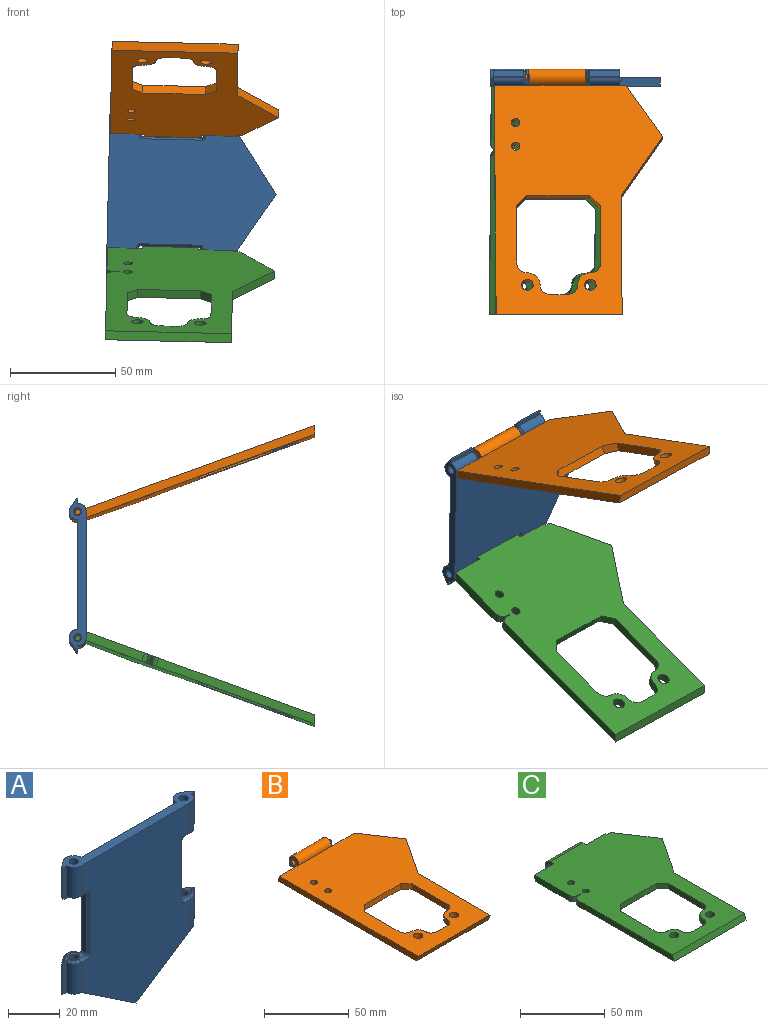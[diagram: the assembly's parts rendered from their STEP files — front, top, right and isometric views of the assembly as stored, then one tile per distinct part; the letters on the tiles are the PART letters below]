
ASSEMBLY  parts=3 mates=2
PART A: 75 faces, bbox 72.4x8x80 mm
  f0: cylinder r=4mm len=14.25mm, axis (0,0,1), area 89.5mm2, adj f4,f9,f39,f60
  f1: cylinder r=4mm len=14.25mm, axis (0,0,1), area 124.2mm2, adj f5,f20,f38,f43
  f2: cylinder r=4mm len=14.25mm, axis (0,0,1), area 89.5mm2, adj f4,f11,f35,f54
  f3: cylinder r=4mm len=14.25mm, axis (0,0,1), area 124.2mm2, adj f5,f9,f34,f45
  f4: plane 80x60mm, normal (0,-1,0), area 3886.9mm2, adj f0,f2,f7,f8,f9,f18,f21,f55
  f5: plane 80x56.3mm, normal (0,1,0), area 2940.6mm2, adj f1,f3,f8,f9,f10,f11,f12,f13
  f6: cylinder r=1.85mm len=14.75mm, axis (0,0,1), area 171.5mm2, adj f9,f27
  f7: cylinder r=4mm len=14.25mm, axis (0,0,1), area 89.5mm2, adj f4,f9,f33,f53
  f8: plane 30x20mm, normal (-0.55,0,-0.83), area 141mm2, adj f4,f5,f10,f11,f18
  f9: plane 72.36x8mm, normal (0,0,1), area 300.9mm2, adj f0,f3,f4,f5,f6,f7,f16,f17
  f10: cylinder r=1.85mm len=15.98mm, axis (0,0,1), area 173.7mm2, adj f5,f8,f11,f26
  f11: plane 10.18x8mm, normal (0,0,-1), area 33.1mm2, adj f2,f5,f8,f10,f12,f35,f36,f50
  f12: cylinder r=4mm len=14.25mm, axis (0,0,1), area 124.2mm2, adj f5,f11,f36,f47
  f13: plane 8.75x6mm, normal (0,0,-1), area 16.5mm2, adj f5,f27,f32,f33,f45,f46,f53,f55
  f14: plane 8.75x6mm, normal (0,0,1), area 16.5mm2, adj f5,f26,f31,f35,f47,f48,f54,f56
  f15: plane 28.5x3mm, normal (-1,0,0), area 85.5mm2, adj f5,f31,f32,f59
  f16: cylinder r=1.85mm len=14.75mm, axis (0,0,1), area 171.5mm2, adj f9,f28
  f17: cylinder r=4mm len=14.25mm, axis (0,0,1), area 124.2mm2, adj f5,f9,f40,f41
  f18: plane 30x20mm, normal (0.55,0,-0.83), area 141mm2, adj f4,f5,f8,f19,f20
  f19: cylinder r=1.85mm len=15.98mm, axis (0,0,1), area 173.7mm2, adj f5,f18,f20,f25
  f20: plane 10.18x8mm, normal (0,0,-1), area 33.1mm2, adj f1,f5,f18,f19,f21,f37,f38,f51
  f21: cylinder r=4mm len=14.25mm, axis (0,0,1), area 89.5mm2, adj f4,f20,f37,f61
  f22: plane 8.75x6mm, normal (0,0,-1), area 16.5mm2, adj f5,f28,f29,f39,f41,f42,f60,f62
  f23: plane 8.75x6mm, normal (0,0,1), area 16.5mm2, adj f5,f25,f30,f37,f43,f44,f61,f63
  f24: plane 28.5x3mm, normal (1,0,0), area 85.5mm2, adj f5,f29,f30,f66
  f25: cone r=2.35mm half-angle=45deg, axis (0,0,1), area 9.3mm2, adj f19,f23
  f26: cone r=1.85mm half-angle=45deg, axis (0,0,1), area 9.3mm2, adj f10,f14
  f27: cone r=2.35mm half-angle=45deg, axis (0,0,-1), area 9.3mm2, adj f6,f13
  f28: cone r=1.85mm half-angle=45deg, axis (0,0,-1), area 9.3mm2, adj f16,f22
  f29: cylinder r=0.5mm len=3mm, axis (0,1,0), area 2.4mm2, adj f5,f22,f24,f64
  f30: cylinder r=0.5mm len=3mm, axis (0,-1,0), area 2.4mm2, adj f5,f23,f24,f65
  f31: cylinder r=0.5mm len=3mm, axis (0,-1,0), area 2.4mm2, adj f5,f14,f15,f58
  f32: cylinder r=0.5mm len=3mm, axis (0,1,0), area 2.4mm2, adj f5,f13,f15,f57
  f33: plane 15.25x3mm, normal (0,-1,0), area 30.8mm2, adj f7,f9,f13,f46,f49,f53
  f34: plane 14.25x3.89mm, normal (-0.57,0.82,0), area 67.6mm2, adj f3,f9,f46,f49
  f35: plane 15.25x3mm, normal (0,-1,0), area 30.8mm2, adj f2,f11,f14,f48,f50,f54
  f36: plane 14.25x3.89mm, normal (-0.57,0.82,0), area 67.6mm2, adj f11,f12,f48,f50
  f37: plane 15.25x3mm, normal (0,-1,0), area 30.8mm2, adj f20,f21,f23,f44,f51,f61
  f38: plane 14.25x3.89mm, normal (0.57,0.82,0), area 67.6mm2, adj f1,f20,f44,f51
  f39: plane 15.25x3mm, normal (0,-1,0), area 30.8mm2, adj f0,f9,f22,f42,f52,f60
  f40: plane 14.25x3.89mm, normal (0.57,0.82,0), area 67.6mm2, adj f9,f17,f42,f52
  f41: cone r=4mm half-angle=45deg, axis (0,0,1), area 10.8mm2, adj f5,f17,f22,f42
  f42: plane 4.47x3.28mm, normal (0.4,0.58,-0.71), area 6.7mm2, adj f22,f39,f40,f41,f52
  f43: cone r=3mm half-angle=45deg, axis (0,0,-1), area 10.8mm2, adj f1,f5,f23,f44
  f44: plane 4.47x3.28mm, normal (0.4,0.58,0.71), area 6.7mm2, adj f23,f37,f38,f43,f51
  f45: cone r=3mm half-angle=45deg, axis (0,0,1), area 10.8mm2, adj f3,f5,f13,f46
  f46: plane 4.47x3.28mm, normal (-0.4,0.58,-0.71), area 6.7mm2, adj f13,f33,f34,f45,f49
  f47: cone r=4mm half-angle=45deg, axis (0,0,-1), area 10.8mm2, adj f5,f12,f14,f48
  f48: plane 4.47x3.28mm, normal (-0.4,0.58,0.71), area 6.7mm2, adj f14,f35,f36,f47,f50
  f49: plane 14.82x0.57mm, normal (-0.95,-0.3,0), area 8.7mm2, adj f9,f33,f34,f46
  f50: plane 14.82x0.57mm, normal (-0.95,-0.3,0), area 8.7mm2, adj f11,f35,f36,f48
  f51: plane 14.82x0.57mm, normal (0.95,-0.3,0), area 8.7mm2, adj f20,f37,f38,f44
  f52: plane 14.82x0.57mm, normal (0.95,-0.3,0), area 8.7mm2, adj f9,f39,f40,f42
  f53: cone r=4mm half-angle=45deg, axis (0,0,1), area 7.8mm2, adj f7,f13,f33,f55
  f54: cone r=3mm half-angle=45deg, axis (0,0,-1), area 7.8mm2, adj f2,f14,f35,f56
  f55: plane 3.5x1mm, normal (0,-0.71,-0.71), area 4.9mm2, adj f4,f13,f53,f57
  f56: plane 3.5x1mm, normal (0,-0.71,0.71), area 4.9mm2, adj f4,f14,f54,f58
  f57: cone r=1.5mm half-angle=45deg, axis (0,-1,0), area 2.2mm2, adj f4,f32,f55,f59
  f58: cone r=1.5mm half-angle=45deg, axis (0,-1,0), area 2.2mm2, adj f4,f31,f56,f59
  f59: plane 28.5x1mm, normal (-0.71,-0.71,0), area 40.3mm2, adj f4,f15,f57,f58
  f60: cone r=3mm half-angle=45deg, axis (0,0,1), area 7.8mm2, adj f0,f22,f39,f62
  f61: cone r=4mm half-angle=45deg, axis (0,0,-1), area 7.8mm2, adj f21,f23,f37,f63
  f62: plane 3.5x1mm, normal (0,-0.71,-0.71), area 4.9mm2, adj f4,f22,f60,f64
  f63: plane 3.5x1mm, normal (0,-0.71,0.71), area 4.9mm2, adj f4,f23,f61,f65
  f64: cone r=1.5mm half-angle=45deg, axis (0,-1,0), area 2.2mm2, adj f4,f29,f62,f66
  f65: cone r=1.5mm half-angle=45deg, axis (0,-1,0), area 2.2mm2, adj f4,f30,f63,f66
  f66: plane 28.5x1mm, normal (0.71,-0.71,0), area 40.3mm2, adj f4,f24,f64,f65
  f67: cylinder r=15.25mm len=30.5mm, axis (0,1,0), area 143.7mm2, adj f68,f73
  f68: cone r=15.75mm half-angle=45deg, axis (0,1,0), area 68.9mm2, adj f5,f67
  f69: plane 30.1x30.1mm, normal (0,1,0), area 626.6mm2, adj f73,f74
  f70: plane 9x9mm, normal (0,1,0), area 63.6mm2, adj f71
  f71: cone r=4.5mm half-angle=45deg, axis (0,-1,0), area 21.1mm2, adj f70,f72
  f72: cylinder r=5mm len=10mm, axis (0,1,0), area 47.1mm2, adj f71,f74
  f73: cone r=15.25mm half-angle=45deg, axis (0,1,0), area 26.9mm2, adj f67,f69
  f74: cone r=5mm half-angle=45deg, axis (0,-1,0), area 9.1mm2, adj f69,f72
PART B: 41 faces, bbox 80x124x8.2 mm
  f0: plane 8x4mm, normal (0,1,0), area 32mm2, adj f5,f13,f38,f39
  f1: plane 16.45x0.8mm, normal (0,1,0), area 13.1mm2, adj f4,f5,f19,f25
  f2: plane 8x7.96mm, normal (1,0,0), area 37.2mm2, adj f6,f13,f22,f24
  f3: plane 8x7.96mm, normal (-1,0,0), area 37.2mm2, adj f6,f13,f23,f25
  f4: plane 117.16x4mm, normal (-1,0,0), area 463mm2, adj f1,f5,f13,f19,f30
  f5: plane 116x80mm, normal (0,0,1), area 5755mm2, adj f0,f1,f4,f6,f7,f8,f9,f10
  f6: cylinder r=4mm len=27.11mm, axis (-1,0,0), area 509mm2, adj f2,f3,f5,f13,f24,f25
  f7: plane 29x4mm, normal (1,0,0), area 116mm2, adj f5,f13,f32,f40
  f8: plane 30x4mm, normal (0,-1,0), area 120mm2, adj f5,f13,f31,f32
  f9: plane 29x4mm, normal (-1,0,0), area 116mm2, adj f5,f13,f31,f37
  f10: plane 60x4mm, normal (1,0,0), area 237.1mm2, adj f5,f11,f13,f30
  f11: plane 30x20mm, normal (0.83,-0.55,0), area 144.2mm2, adj f5,f10,f12,f13
  f12: plane 26x17.33mm, normal (0.83,0.55,0), area 125mm2, adj f5,f11,f13,f14
  f13: plane 118.54x80mm, normal (0,0,-1), area 5814.2mm2, adj f0,f2,f3,f4,f6,f7,f8,f9
  f14: plane 19.11x4mm, normal (0,1,0), area 23.7mm2, adj f5,f12,f13,f20,f21,f24
  f15: cylinder r=1.5mm len=3mm, axis (-1,0,0), area 21.2mm2, adj f22,f26
  f16: plane 2.5x2.5mm, normal (1,0,0), area 4.9mm2, adj f26
  f17: cylinder r=1.5mm len=3mm, axis (1,0,0), area 21.2mm2, adj f23,f27
  f18: plane 2.5x2.5mm, normal (-1,0,0), area 4.9mm2, adj f27
  f19: plane 16x3.2mm, normal (0,0.94,0.34), area 54.5mm2, adj f1,f4,f13,f25
  f20: plane 16x3.2mm, normal (0,0.94,0.34), area 54.5mm2, adj f13,f14,f21,f24
  f21: plane 3.2x1.16mm, normal (1,0,0), area 1.9mm2, adj f13,f14,f20
  f22: torus R=2mm, axis (-1,0,0), area 8.3mm2, adj f2,f15
  f23: torus R=2mm, axis (-1,0,0), area 8.3mm2, adj f3,f17
  f24: cylinder r=0.5mm len=4.73mm, axis (0,-0.34,0.94), area 3.1mm2, adj f2,f6,f13,f14,f20
  f25: cylinder r=0.5mm len=4.73mm, axis (0,0.34,-0.94), area 3.1mm2, adj f1,f3,f6,f13,f19
  f26: cone r=1.5mm half-angle=45deg, axis (-1,0,0), area 3.1mm2, adj f15,f16
  f27: cone r=1.5mm half-angle=45deg, axis (1,0,0), area 3.1mm2, adj f17,f18
  f28: cylinder r=2mm len=4mm, axis (0,0,-1), area 50.3mm2, adj f5,f13
  f29: cylinder r=2mm len=4mm, axis (0,0,-1), area 50.3mm2, adj f5,f13
  f30: plane 60x4mm, normal (0,-0.94,-0.34), area 255.4mm2, adj f4,f5,f10,f13
  f31: plane 5x5mm, normal (-0.71,-0.71,0), area 28.3mm2, adj f5,f8,f9,f13
  f32: plane 5x5mm, normal (0.71,-0.71,0), area 28.3mm2, adj f5,f7,f8,f13
  f33: cylinder r=6mm len=6mm, axis (0,0,1), area 37.7mm2, adj f5,f13,f39,f40
  f34: cylinder r=2.75mm len=5.5mm, axis (0,0,1), area 69.1mm2, adj f5,f13
  f35: cylinder r=6mm len=6mm, axis (0,0,1), area 37.7mm2, adj f5,f13,f37,f38
  f36: cylinder r=2.75mm len=5.5mm, axis (0,0,1), area 69.1mm2, adj f5,f13
  f37: cylinder r=5mm len=5mm, axis (0,0,1), area 31.4mm2, adj f5,f9,f13,f35
  f38: cylinder r=5mm len=5mm, axis (0,0,1), area 31.4mm2, adj f0,f5,f13,f35
  f39: cylinder r=5mm len=5mm, axis (0,0,1), area 31.4mm2, adj f0,f5,f13,f33
  f40: cylinder r=5mm len=5mm, axis (0,0,1), area 31.4mm2, adj f5,f7,f13,f33
PART C: 55 faces, bbox 80x124x8.2 mm
  f0: plane 8x4mm, normal (0,1,0), area 32mm2, adj f2,f3,f49,f50
  f1: plane 29.57x4mm, normal (-1,0,0), area 115.5mm2, adj f2,f3,f6,f20,f42
  f2: plane 116x80mm, normal (0,0,-1), area 5746.4mm2, adj f0,f1,f4,f5,f6,f9,f10,f11
  f3: plane 118.54x80mm, normal (0,0,1), area 5805.6mm2, adj f0,f1,f4,f5,f7,f8,f9,f10
  f4: plane 29x4mm, normal (1,0,0), area 116mm2, adj f2,f3,f33,f51
  f5: plane 29x4mm, normal (-1,0,0), area 116mm2, adj f2,f3,f32,f48
  f6: plane 16.45x0.8mm, normal (0,1,0), area 13.1mm2, adj f1,f2,f20,f24
  f7: plane 8x7.96mm, normal (1,0,0), area 37.2mm2, adj f3,f10,f23,f26
  f8: plane 8x7.96mm, normal (-1,0,0), area 37.2mm2, adj f3,f10,f24,f25
  f9: plane 80.41x4mm, normal (-1,0,0), area 318.7mm2, adj f2,f3,f31,f41
  f10: cylinder r=4mm len=27.11mm, axis (-1,0,0), area 509mm2, adj f2,f3,f7,f8,f23,f24
  f11: plane 30x4mm, normal (0,-1,0), area 120mm2, adj f2,f3,f32,f33
  f12: plane 60x4mm, normal (1,0,0), area 237.1mm2, adj f2,f3,f13,f31
  f13: plane 30x20mm, normal (0.83,-0.55,0), area 144.2mm2, adj f2,f3,f12,f14
  f14: plane 26x17.33mm, normal (0.83,0.55,0), area 125mm2, adj f2,f3,f13,f15
  f15: plane 19.11x4mm, normal (0,1,0), area 23.7mm2, adj f2,f3,f14,f21,f22,f23
  f16: cylinder r=1.5mm len=3mm, axis (-1,0,0), area 21.2mm2, adj f26,f28
  f17: plane 2.5x2.5mm, normal (1,0,0), area 4.9mm2, adj f28
  f18: cylinder r=1.5mm len=3mm, axis (1,0,0), area 21.2mm2, adj f25,f27
  f19: plane 2.5x2.5mm, normal (-1,0,0), area 4.9mm2, adj f27
  f20: plane 16x3.2mm, normal (0,0.94,-0.34), area 54.5mm2, adj f1,f3,f6,f24
  f21: plane 16x3.2mm, normal (0,0.94,-0.34), area 54.5mm2, adj f3,f15,f22,f23
  f22: plane 3.2x1.16mm, normal (1,0,0), area 1.9mm2, adj f3,f15,f21
  f23: cylinder r=0.5mm len=4.73mm, axis (0,-0.34,-0.94), area 3.1mm2, adj f3,f7,f10,f15,f21
  f24: cylinder r=0.5mm len=4.73mm, axis (0,0.34,0.94), area 3.1mm2, adj f3,f6,f8,f10,f20
  f25: torus R=2mm, axis (-1,0,0), area 8.3mm2, adj f8,f18
  f26: torus R=2mm, axis (-1,0,0), area 8.3mm2, adj f7,f16
  f27: cone r=1.25mm half-angle=45deg, axis (1,0,0), area 3.1mm2, adj f18,f19
  f28: cone r=1.25mm half-angle=45deg, axis (-1,0,0), area 3.1mm2, adj f16,f17
  f29: cylinder r=2mm len=4mm, axis (0,0,-1), area 50.3mm2, adj f2,f3
  f30: cylinder r=2mm len=4mm, axis (0,0,-1), area 50.3mm2, adj f2,f3
  f31: plane 60x4mm, normal (0,-0.94,0.34), area 255.4mm2, adj f2,f3,f9,f12
  f32: plane 5x5mm, normal (-0.71,-0.71,0), area 28.3mm2, adj f2,f3,f5,f11
  f33: plane 5x5mm, normal (0.71,-0.71,0), area 28.3mm2, adj f2,f3,f4,f11
  f34: plane 4x0.71mm, normal (-0.33,0.94,0), area 3mm2, adj f2,f3,f53,f54
  f35: plane 4x1.74mm, normal (0,1,0), area 7mm2, adj f2,f3,f40,f53
  f36: plane 4x1.74mm, normal (0,-1,0), area 7mm2, adj f2,f3,f43,f52
  f37: plane 4x0.71mm, normal (-0.33,-0.94,0), area 3mm2, adj f2,f3,f52,f54
  f38: plane 4x0.24mm, normal (-0.71,-0.71,0), area 1.4mm2, adj f2,f3,f42,f43
  f39: plane 4x0.24mm, normal (-0.71,0.71,0), area 1.4mm2, adj f2,f3,f40,f41
  f40: cylinder r=3mm len=4mm, axis (0,0,1), area 9.4mm2, adj f2,f3,f35,f39
  f41: cylinder r=3mm len=4mm, axis (0,0,1), area 9.4mm2, adj f2,f3,f9,f39
  f42: cylinder r=3mm len=4mm, axis (0,0,1), area 9.4mm2, adj f1,f2,f3,f38
  f43: cylinder r=3mm len=4mm, axis (0,0,-1), area 9.4mm2, adj f2,f3,f36,f38
  f44: cylinder r=6mm len=6mm, axis (0,0,1), area 37.7mm2, adj f2,f3,f50,f51
  f45: cylinder r=2.75mm len=5.5mm, axis (0,0,1), area 69.1mm2, adj f2,f3
  f46: cylinder r=6mm len=6mm, axis (0,0,1), area 37.7mm2, adj f2,f3,f48,f49
  f47: cylinder r=2.75mm len=5.5mm, axis (0,0,1), area 69.1mm2, adj f2,f3
  f48: cylinder r=5mm len=5mm, axis (0,0,1), area 31.4mm2, adj f2,f3,f5,f46
  f49: cylinder r=5mm len=5mm, axis (0,0,1), area 31.4mm2, adj f0,f2,f3,f46
  f50: cylinder r=5mm len=5mm, axis (0,0,1), area 31.4mm2, adj f0,f2,f3,f44
  f51: cylinder r=5mm len=5mm, axis (0,0,1), area 31.4mm2, adj f2,f3,f4,f44
  f52: cylinder r=0.1mm len=4mm, axis (0,0,-1), area 0.1mm2, adj f2,f3,f36,f37
  f53: cylinder r=0.1mm len=4mm, axis (0,0,1), area 0.1mm2, adj f2,f3,f34,f35
  f54: cylinder r=0.1mm len=4mm, axis (0,0,1), area 1mm2, adj f2,f3,f34,f37
PLACE A rot(axis=(0,-1,0),88.7deg) t=(-34.98,0,-29.21)mm
PLACE B rot(axis=(-1,0.06,0.01),20deg) t=(-33.53,-2.74,23.25)mm
PLACE C rot(axis=(1,0.06,-0.01),20deg) t=(-34.73,0,-29.21)mm
MATE revolute A.f6 <-> C.f10  axis (-1,0,0.02) through (9.76,0,-30.23)mm
MATE revolute A.f25 <-> B.f26  axis (-1,0,0.02) through (11.13,0,29.75)mm
